# Revit family: Crest FBNT Boiler_Revit 2014
name_source: partatom
category: Mechanical Equipment
revit_build: Autodesk Revit 2014 (Build: 20130308_1515(x64)
units: mm (PartAtom-declared; Revit-internal decimal feet)

## types (6) — shared parameters
# of Electrical Connections = 1
A_WIDTH = 30"
Back Clearance = 24"
Drain Depth = 4"
Front Clearance = 30"
Fuel Type = Natural or LP
HEIGHT = 78"
Left Clearance = 24"
Manufacturer = Lochinvar
Right Clearance = 24"
SES BIM Studio # = 14 0649 04-1
Top Clearance = 24"
URL = http://www.lochinvar.com
Voltage/Control = 24
Voltage/Heater = 120/1PH

## per-type parameters (varying)
- FBN0751: AIR INTAKE SIZE=6"; Air Intake Radius=3"; C_Depth to Vent=51"; D_Air Inlet Offset=13"; Depth=49"; Description=CREST Boiler; Drain Offset=57"; E_Air Intake Offset=8 3/4"; FUEL TYPE=Natural Gas; F_Gas Conn Height=23 3/4"; GALLON CAPACITY=73; GAS CONN SIZE=1 1/4"; G_Width to Gas=26 3/4"; Gas Conn Radius=5/8"; H_ Vent Offset=5 1/8"; INPUT RATE (BTUH)=750,000; J_Water Conn Offset=57 5/8"; K_Water Inlet Height=11 7/8"; L_Water Outlet Height=66 1/8"; MODEL NO.=FBN750; Model=FBN750; Total Amps=5; VENT SIZE=6"; Vent Radius=3"; WATER CONN SIZE=3"; Water Conn Radius=1 1/2"
- FBN1001: AIR INTAKE SIZE=6"; Air Intake Radius=3"; C_Depth to Vent=51"; D_Air Inlet Offset=13"; Depth=49"; Description=CREST Boiler; Drain Offset=56 1/4"; E_Air Intake Offset=8 3/4"; FUEL TYPE=NATURAL GAS; F_Gas Conn Height=23 1/8"; GALLON CAPACITY=77; GAS CONN SIZE=1 1/4"; G_Width to Gas=26 3/4"; Gas Conn Radius=5/8"; H_ Vent Offset=5 1/8"; INPUT RATE (BTUH)=1,000,000; J_Water Conn Offset=57 5/8"; K_Water Inlet Height=11 7/8"; L_Water Outlet Height=66 1/8"; MODEL NO.=FBN1001; Model=FBN1001; Total Amps=6; VENT SIZE=6"; Vent Radius=3"; WATER CONN SIZE=3"; Water Conn Radius=1 1/2"
- FBN1251: AIR INTAKE SIZE=6"; Air Intake Radius=3"; C_Depth to Vent=51 3/8"; D_Air Inlet Offset=13"; Depth=49 3/8"; Description=CREST Condensing Boiler; Drain Offset=61 7/8"; E_Air Intake Offset=8 3/4"; FUEL TYPE=NATURAL GAS; F_Gas Conn Height=21 5/8"; GALLON CAPACITY=87; GAS CONN SIZE=1 1/4"; G_Width to Gas=26 3/4"; Gas Conn Radius=5/8"; H_ Vent Offset=6 1/2"; INPUT RATE (BTUH)=1,250,000; J_Water Conn Offset=57 3/4"; K_Water Inlet Height=11 7/8"; L_Water Outlet Height=66 1/8"; MODEL NO.=FBN1251; Model=FBN1251; Total Amps=7; VENT SIZE=8"; Vent Radius=4"; WATER CONN SIZE=3"; Water Conn Radius=1 1/2"
- FBN1501: AIR INTAKE SIZE=8"; Air Intake Radius=4"; C_Depth to Vent=62 3/8"; D_Air Inlet Offset=15 7/8"; Depth=60 3/8"; Description=CREST Condensing Boiler; Drain Offset=61 7/8"; E_Air Intake Offset=9"; FUEL TYPE=NATURAL GAS; F_Gas Conn Height=27 7/8"; GALLON CAPACITY=94; GAS CONN SIZE=1 1/2"; G_Width to Gas=26 7/8"; Gas Conn Radius=3/4"; H_ Vent Offset=5 1/8"; INPUT RATE (BTUH)=1,500,000; J_Water Conn Offset=68"; K_Water Inlet Height=12 3/8"; L_Water Outlet Height=65 3/8"; MODEL NO.=FBN1501; Model=FBN1501; Total Amps=10; VENT SIZE=8"; Vent Radius=4"; WATER CONN SIZE=4"; Water Conn Radius=2"
- FBN1751: AIR INTAKE SIZE=8"; Air Intake Radius=4"; C_Depth to Vent=61 1/2"; D_Air Inlet Offset=15 7/8"; Depth=59 1/2"; Description=CREST Condensing Boiler; Drain Offset=61 7/8"; E_Air Intake Offset=9"; FUEL TYPE=NATURAL GAS; F_Gas Conn Height=27 1/8"; GALLON CAPACITY=106; GAS CONN SIZE=1 1/2"; G_Width to Gas=27"; Gas Conn Radius=3/4"; H_ Vent Offset=5 1/8"; INPUT RATE (BTUH)=1,750,000; J_Water Conn Offset=68"; K_Water Inlet Height=12 3/8"; L_Water Outlet Height=65 3/8"; MODEL NO.=FBN1751; Model=FBN1751; Total Amps=10; VENT SIZE=8"; Vent Radius=4"; WATER CONN SIZE=4"; Water Conn Radius=2"
- FBN2001: AIR INTAKE SIZE=8"; Air Intake Radius=4"; C_Depth to Vent=61 1/2"; D_Air Inlet Offset=15 7/8"; Depth=59 1/2"; Description=CREST Condensing Boiler; Drain Offset=61 7/8"; E_Air Intake Offset=9"; FUEL TYPE=NATURAL GAS; F_Gas Conn Height=26 3/4"; GALLON CAPACITY=111; GAS CONN SIZE=1 1/2"; G_Width to Gas=27"; Gas Conn Radius=3/4"; H_ Vent Offset=5 1/8"; INPUT RATE (BTUH)=2,000,000; J_Water Conn Offset=68"; K_Water Inlet Height=12 3/8"; L_Water Outlet Height=65 3/8"; MODEL NO.=FBN2001; Model=FBN2001; Total Amps=10; VENT SIZE=8"; Vent Radius=4"; WATER CONN SIZE=4"; Water Conn Radius=2"

## geometry (parser evidence)
native form markers: Sweep x1
no freeform markers — native parametric forms only
